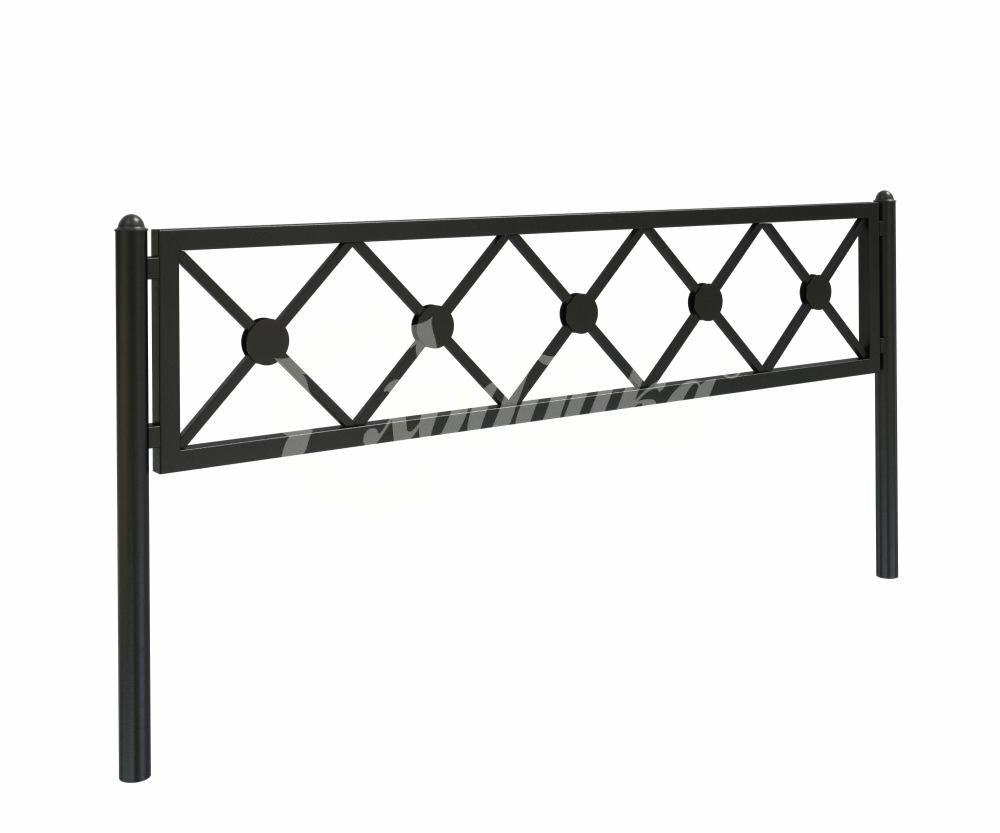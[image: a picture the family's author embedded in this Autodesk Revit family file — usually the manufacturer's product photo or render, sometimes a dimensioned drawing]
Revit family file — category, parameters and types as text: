
# Revit family: 12615 Ограждение стальное 0.7 Хоббика
name_source: partatom
category: Антураж
revit_build: Autodesk Revit 2018 (Build: 20180423_1000(x64)
units: mm (PartAtom-declared; Revit-internal decimal feet)

## family parameters
Всегда вертикально = Да
Источник визуального образа = Геометрия семейства
На основе рабочей плоскости = Нет
Общий = Нет
При загрузке вырезать с полостями = Нет
Точка расчета площади = Нет

## types (2) — shared parameters
URL = https://hobbyka.ru
Артикул товара = Арт. 12615
Высота секции = 450 мм
Высота стойки = 1030 мм
Группа модели = Тротуарные столбики и ограждения
Диаметр стойки = 57 мм
Изготовитель = ООО «Хоббика»
Изображение типоразмера = Ограждение стальное 0.7 Арт 12615.jpg
Материал изделия = Сталь
Цвет каркаса = Сталь

## per-type parameters (varying)
| type | Высота | Длина | Описание | Секция | Стойка | Ширина |
| Секция | 450 мм | 2040 мм | Ограждение стальное 0.7. Секция | Да | Нет | 40 мм |
| Стойка | 1030 мм | 57 мм | Ограждение стальное 0.7. Стойка | Нет | Да | 57 мм |
